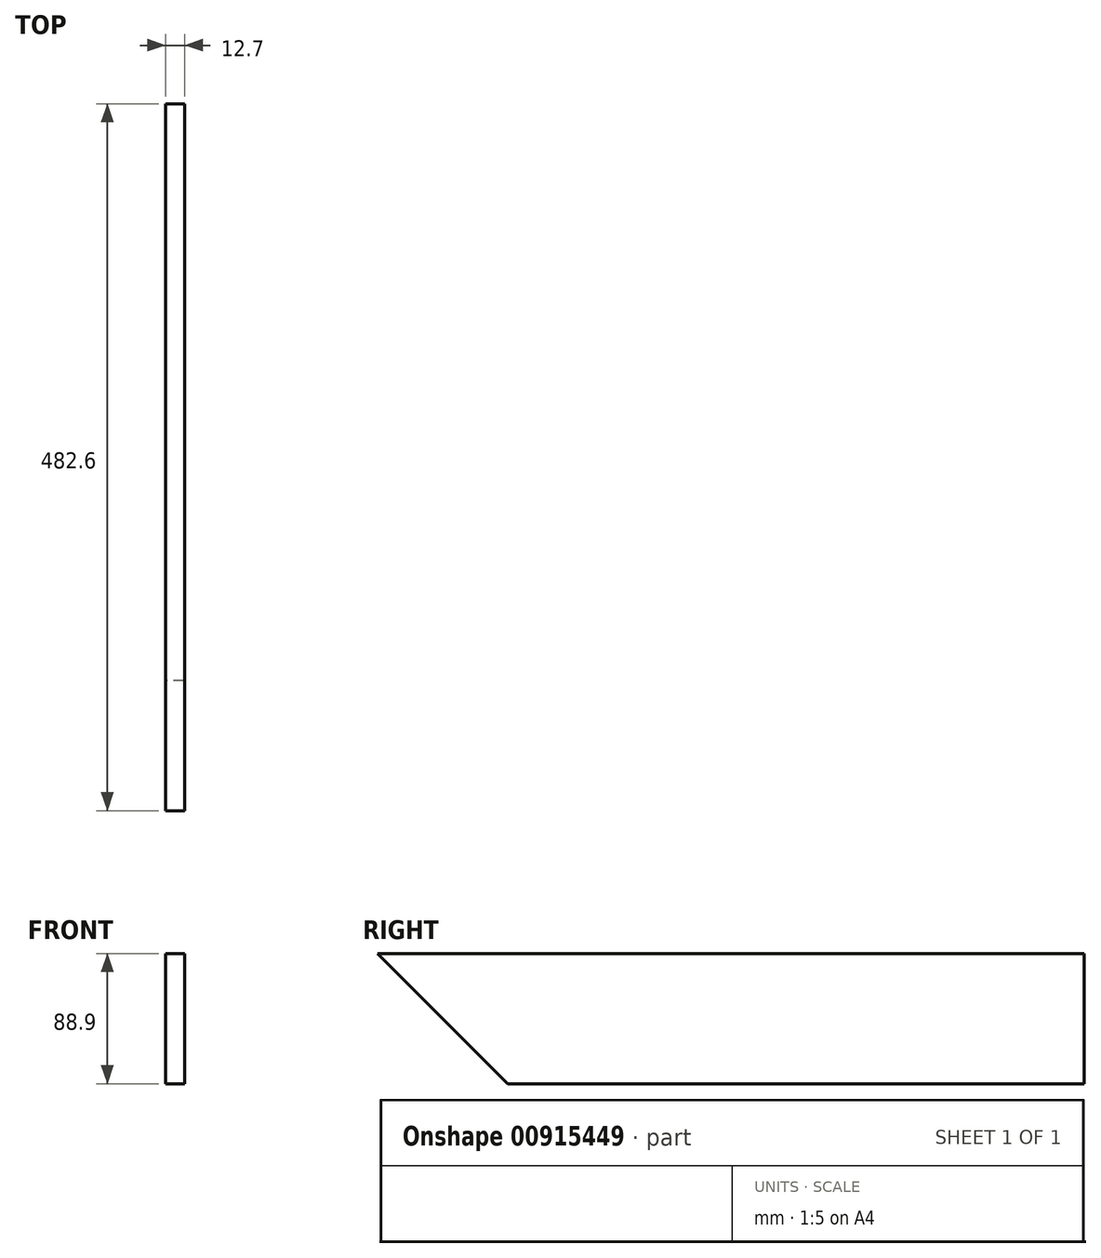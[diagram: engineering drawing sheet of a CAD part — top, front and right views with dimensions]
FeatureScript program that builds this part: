
annotation { "Feature Type Name" : "Feature", "Feature Type Description" : "" }
export const myFeature = defineFeature(function(context is Context, id is Id, definition is map)
    precondition{}
    {
        {
            var Q0;
            Q0=qCreatedBy(makeId("Right.planeOp"),FACE);
            var sketch = newSketch(context, id + "F0", { "sketchPlane" : qUnion([Q0])});
            skLineSegment(sketch, "E0.bottom", {"start": v(241.3, 44.45) * mm, "end": v(-241.3, 44.45) * mm});
            skLineSegment(sketch, "E0.top", {"start": v(241.3, -44.45) * mm, "end": v(-152.4, -44.45) * mm});
            skLineSegment(sketch, "E0.left", {"start": v(241.3, 44.45) * mm, "end": v(241.3, -44.45) * mm});
            skPoint(sketch, "E0.middle", {"position": v(0, 0) * mm});
            skLineSegment(sketch, "E1", {"start": v(-241.3, 44.45) * mm, "end": v(-152.4, -44.45) * mm});
            skSolve(sketch);
        }
        {
            var Q0;
            Q0=makeQuery(id+"F0.imprint","IMPRINT",FACE,{"disambiguationData":[TD([[makeQuery(id+"F0.imprint","IMPRINT",EDGE,{"derivedFrom":sQuery(id+"F0.wireOp",EDGE,"E0.bottom")}),1.0]])]});
            extrude(context, id + "F1", {"entities" : qUnion([Q0]), "depth" : 12.7 * mm, "offsetDistance" : 25.4 * mm});
        }
    });
